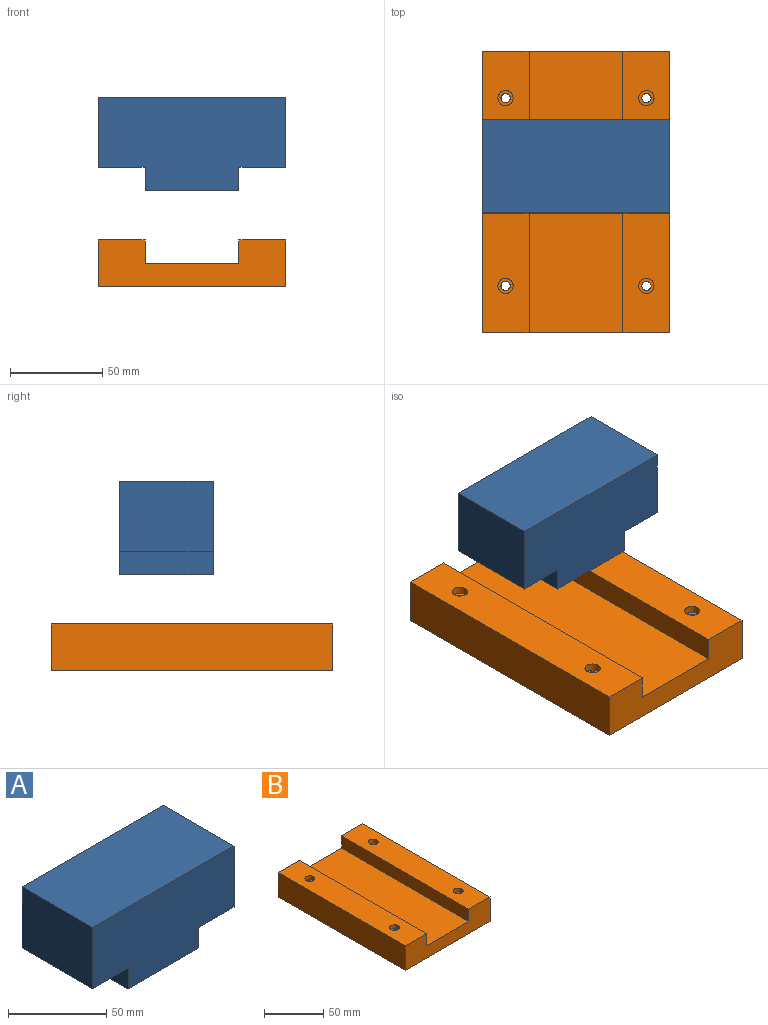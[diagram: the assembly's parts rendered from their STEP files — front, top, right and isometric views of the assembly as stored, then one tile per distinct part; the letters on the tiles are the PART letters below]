
ASSEMBLY  parts=2 mates=1
PART A: 10 faces, bbox 101.6x50.8x50.8 mm
  f0: plane 50.8x38.1mm, normal (1,0,0), area 1935.5mm2, adj f1,f7,f8,f9
  f1: plane 101.6x50.8mm, normal (0,0,1), area 5161.3mm2, adj f0,f2,f8,f9
  f2: plane 50.8x38.1mm, normal (-1,0,0), area 1935.5mm2, adj f1,f3,f8,f9
  f3: plane 50.8x25.4mm, normal (0,0,-1), area 1290.3mm2, adj f2,f4,f8,f9
  f4: plane 50.8x12.7mm, normal (-1,0,0), area 645.2mm2, adj f3,f5,f8,f9
  f5: plane 50.8x50.8mm, normal (0,0,-1), area 2580.6mm2, adj f4,f6,f8,f9
  f6: plane 50.8x12.7mm, normal (1,0,0), area 645.2mm2, adj f5,f7,f8,f9
  f7: plane 50.8x25.4mm, normal (0,0,-1), area 1290.3mm2, adj f0,f6,f8,f9
  f8: plane 101.6x50.8mm, normal (0,-1,0), area 4516.1mm2, adj f0,f1,f2,f3,f4,f5,f6,f7
  f9: plane 101.6x50.8mm, normal (0,1,0), area 4516.1mm2, adj f0,f1,f2,f3,f4,f5,f6,f7
PART B: 22 faces, bbox 101.6x152.4x25.4 mm
  f0: plane 152.4x12.7mm, normal (1,0,0), area 1935.5mm2, adj f1,f7,f8,f9
  f1: plane 152.4x25.4mm, normal (0,0,1), area 3764mm2, adj f0,f2,f8,f9,f12,f21
  f2: plane 152.4x25.4mm, normal (-1,0,0), area 3871mm2, adj f1,f3,f8,f9
  f3: plane 152.4x101.6mm, normal (0,0,-1), area 15405.3mm2, adj f2,f4,f8,f9,f10,f13,f16,f19
  f4: plane 152.4x25.4mm, normal (1,0,0), area 3871mm2, adj f3,f5,f8,f9
  f5: plane 152.4x25.4mm, normal (0,0,1), area 3764mm2, adj f4,f6,f8,f9,f15,f18
  f6: plane 152.4x12.7mm, normal (-1,0,0), area 1935.5mm2, adj f5,f7,f8,f9
  f7: plane 152.4x50.8mm, normal (0,0,1), area 7741.9mm2, adj f0,f6,f8,f9
  f8: plane 101.6x25.4mm, normal (0,-1,0), area 1935.5mm2, adj f0,f1,f2,f3,f4,f5,f6,f7
  f9: plane 101.6x25.4mm, normal (0,1,0), area 1935.5mm2, adj f0,f1,f2,f3,f4,f5,f6,f7
  f10: cylinder r=2.5mm len=21.4mm, axis (0,0,1), area 336.2mm2, adj f3,f11
  f11: plane 8.25x8.25mm, normal (0,0,1), area 33.8mm2, adj f10,f12
  f12: cylinder r=4.12mm len=8.25mm, axis (0,0,1), area 103.7mm2, adj f1,f11
  f13: cylinder r=2.5mm len=21.4mm, axis (0,0,1), area 336.2mm2, adj f3,f14
  f14: plane 8.25x8.25mm, normal (0,0,1), area 33.8mm2, adj f13,f15
  f15: cylinder r=4.12mm len=8.25mm, axis (0,0,1), area 103.7mm2, adj f5,f14
  f16: cylinder r=2.5mm len=21.4mm, axis (0,0,1), area 336.2mm2, adj f3,f17
  f17: plane 8.25x8.25mm, normal (0,0,1), area 33.8mm2, adj f16,f18
  f18: cylinder r=4.12mm len=8.25mm, axis (0,0,1), area 103.7mm2, adj f5,f17
  f19: cylinder r=2.5mm len=21.4mm, axis (0,0,1), area 336.2mm2, adj f3,f20
  f20: plane 8.25x8.25mm, normal (0,0,1), area 33.8mm2, adj f19,f21
  f21: cylinder r=4.12mm len=8.25mm, axis (0,0,1), area 103.7mm2, adj f1,f20
PLACE A t=(-13.39,57.98,5.6)mm
PLACE B t=(-13.39,44.07,-33.62)mm
MATE planar A.f6 <-> B.f6  axis (1,0,0) through (12.01,57.98,24.65)mm
